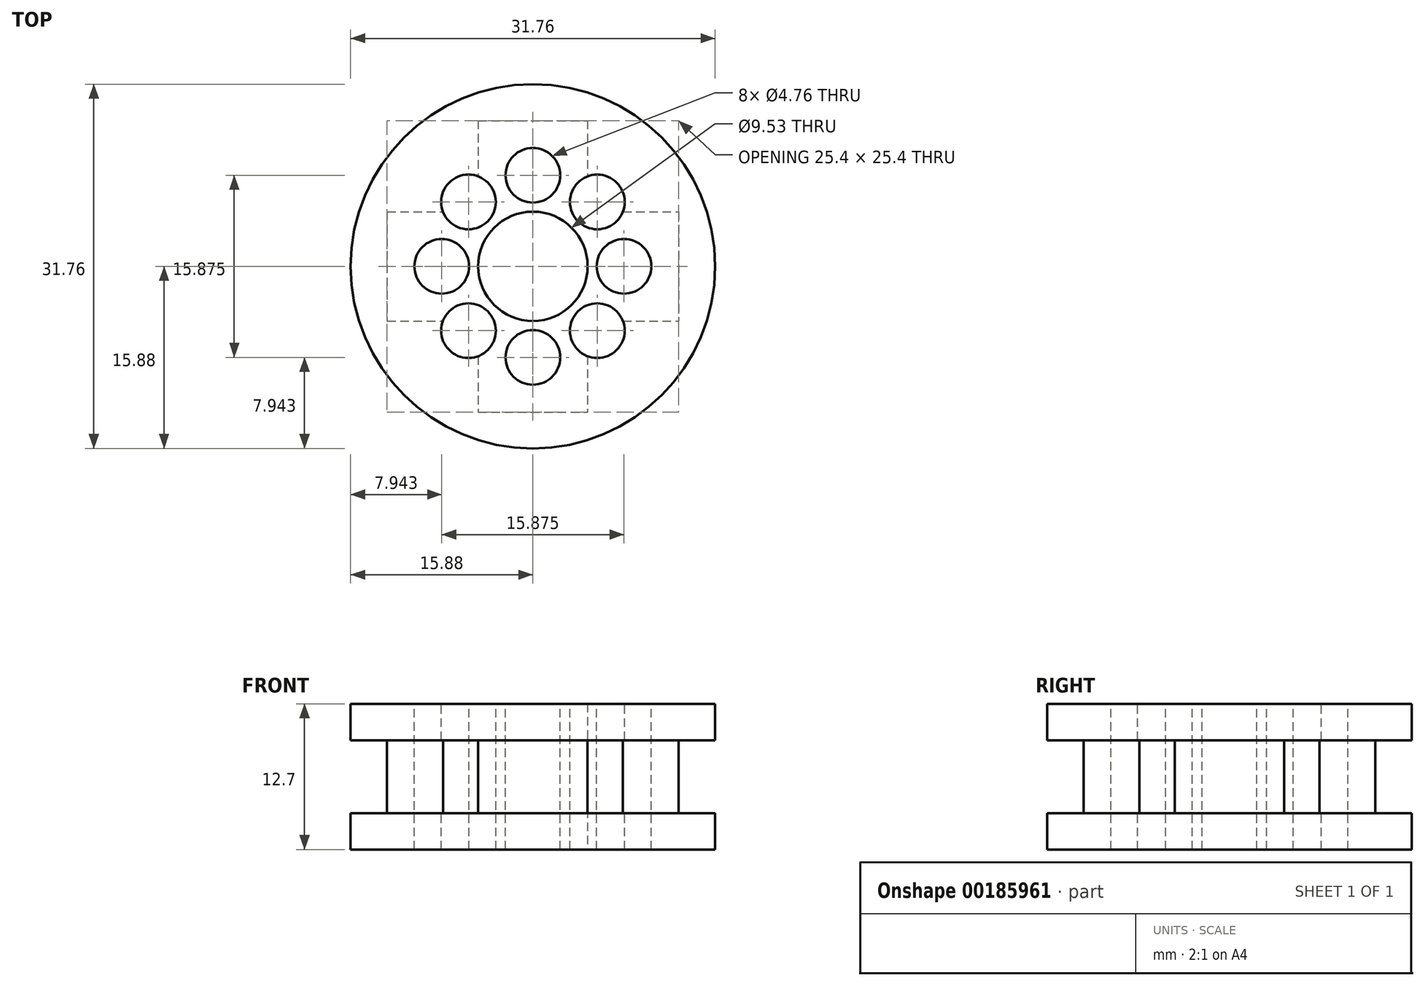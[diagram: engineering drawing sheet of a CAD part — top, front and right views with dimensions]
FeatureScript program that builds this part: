
annotation { "Feature Type Name" : "Feature", "Feature Type Description" : "" }
export const myFeature = defineFeature(function(context is Context, id is Id, definition is map)
    precondition{}
    {
        {
            var Q0;
            Q0=qCreatedBy(makeId("Top.planeOp"),FACE);
            var sketch = newSketch(context, id + "F0", { "sketchPlane" : qUnion([Q0])});
            skCircle(sketch, "E0", {"center": v(0, 0) * mm, "radius": 15.88 * mm});
            skCircle(sketch, "E1", {"center": v(0, 0) * mm, "radius": 4.76 * mm});
            skSolve(sketch);
        }
        {
            var Q0;
            Q0 = qSketchRegion(id + "F0", true);
            extrude(context, id + "F1", {"entities" : qUnion([Q0]), "depth" : 3.17 * mm});
        }
        {
            var Q0;
            Q0=makeQuery(id+"F1.opExtrude","CAP_FACE",FACE,{"disambiguationData":[OSD([sQuery(id+"F0.wireOp",EDGE,"E0"),sQuery(id+"F0.wireOp",EDGE,"E1")])],"isStart":false});
            var sketch = newSketch(context, id + "F2", { "sketchPlane" : qUnion([Q0])});
            skCircle(sketch, "E2", {"center": v(0, 0) * mm, "radius": 4.76 * mm});
            skLineSegment(sketch, "E3.bottom", {"start": v(-4.76, 12.7) * mm, "end": v(4.76, 12.7) * mm});
            skLineSegment(sketch, "E3.top", {"start": v(-4.76, -12.7) * mm, "end": v(4.76, -12.7) * mm});
            skLineSegment(sketch, "E3.left", {"start": v(-4.76, 12.7) * mm, "end": v(-4.76, -12.7) * mm});
            skLineSegment(sketch, "E3.right", {"start": v(4.76, 12.7) * mm, "end": v(4.76, -12.7) * mm});
            skLineSegment(sketch, "E4.bottom", {"start": v(-12.7, 4.76) * mm, "end": v(12.7, 4.76) * mm});
            skLineSegment(sketch, "E4.top", {"start": v(-12.7, -4.76) * mm, "end": v(12.7, -4.76) * mm});
            skLineSegment(sketch, "E4.left", {"start": v(-12.7, 4.76) * mm, "end": v(-12.7, -4.76) * mm});
            skLineSegment(sketch, "E4.right", {"start": v(12.7, 4.76) * mm, "end": v(12.7, -4.76) * mm});
            skSolve(sketch);
        }
        {
            var Q0;
            Q0 = qSketchRegion(id + "F2", true);
            extrude(context, id + "F3", {"entities" : qUnion([Q0]), "operationType" : NewBodyOperationType.ADD, "depth" : 6.35 * mm});
        }
        {
            var Q0;
            Q0=makeQuery(id+"F3.opExtrude","CAP_FACE",FACE,{"disambiguationData":[OSD([sQuery(id+"F2.wireOp",EDGE,"E2"),sQuery(id+"F2.wireOp",EDGE,"E3.bottom"),sQuery(id+"F2.wireOp",EDGE,"E3.top"),sQuery(id+"F2.wireOp",EDGE,"E3.left"),sQuery(id+"F2.wireOp",EDGE,"E3.right"),sQuery(id+"F2.wireOp",EDGE,"E4.bottom"),sQuery(id+"F2.wireOp",EDGE,"E4.top"),sQuery(id+"F2.wireOp",EDGE,"E4.left"),sQuery(id+"F2.wireOp",EDGE,"E4.right")])],"isStart":false});
            var sketch = newSketch(context, id + "F4", { "sketchPlane" : qUnion([Q0])});
            skCircle(sketch, "E5", {"center": v(0, 0) * mm, "radius": 15.88 * mm});
            skCircle(sketch, "E6", {"center": v(0, 0) * mm, "radius": 4.76 * mm});
            skSolve(sketch);
        }
        {
            var Q0;
            Q0 = qSketchRegion(id + "F4", true);
            extrude(context, id + "F5", {"entities" : qUnion([Q0]), "operationType" : NewBodyOperationType.ADD, "depth" : 3.17 * mm});
        }
        {
            var Q0;
            Q0=makeQuery(id+"F5.opExtrude","CAP_FACE",FACE,{"disambiguationData":[OSD([sQuery(id+"F4.wireOp",EDGE,"E5"),sQuery(id+"F4.wireOp",EDGE,"E6")])],"isStart":false});
            var sketch = newSketch(context, id + "F6", { "sketchPlane" : qUnion([Q0])});
            skCircle(sketch, "E7", {"center": v(0, 7.94) * mm, "radius": 2.38 * mm});
            skCircle(sketch, "E8.1.0", {"center": v(-5.61, 5.61) * mm, "radius": 2.38 * mm});
            skCircle(sketch, "E8.2.0", {"center": v(-7.94, 0) * mm, "radius": 2.38 * mm});
            skCircle(sketch, "E8.3.0", {"center": v(-5.61, -5.61) * mm, "radius": 2.38 * mm});
            skCircle(sketch, "E8.4.0", {"center": v(0, -7.94) * mm, "radius": 2.38 * mm});
            skCircle(sketch, "E8.5.0", {"center": v(5.61, -5.61) * mm, "radius": 2.38 * mm});
            skCircle(sketch, "E8.6.0", {"center": v(7.94, 0) * mm, "radius": 2.38 * mm});
            skCircle(sketch, "E8.7.0", {"center": v(5.61, 5.61) * mm, "radius": 2.38 * mm});
            skPoint(sketch, "E8.center", {"position": v(0, 0) * mm});
            skSolve(sketch);
        }
        {
            var Q0;
            Q0=makeQuery(id+"F6.imprint","IMPRINT",FACE,{"disambiguationData":[TD([[makeQuery(id+"F6.imprint","IMPRINT",EDGE,{"derivedFrom":sQuery(id+"F6.wireOp",EDGE,"E8.1.0")}),1.0]])]});
            var Q1;
            Q1=makeQuery(id+"F6.imprint","IMPRINT",FACE,{"disambiguationData":[TD([[makeQuery(id+"F6.imprint","IMPRINT",EDGE,{"derivedFrom":sQuery(id+"F6.wireOp",EDGE,"E7")}),1.0]])]});
            var Q2;
            Q2=makeQuery(id+"F6.imprint","IMPRINT",FACE,{"disambiguationData":[TD([[makeQuery(id+"F6.imprint","IMPRINT",EDGE,{"derivedFrom":sQuery(id+"F6.wireOp",EDGE,"E8.7.0")}),1.0]])]});
            var Q3;
            Q3=makeQuery(id+"F6.imprint","IMPRINT",FACE,{"disambiguationData":[TD([[makeQuery(id+"F6.imprint","IMPRINT",EDGE,{"derivedFrom":sQuery(id+"F6.wireOp",EDGE,"E8.6.0")}),1.0]])]});
            var Q4;
            Q4=makeQuery(id+"F6.imprint","IMPRINT",FACE,{"disambiguationData":[TD([[makeQuery(id+"F6.imprint","IMPRINT",EDGE,{"derivedFrom":sQuery(id+"F6.wireOp",EDGE,"E8.5.0")}),1.0]])]});
            var Q5;
            Q5=makeQuery(id+"F6.imprint","IMPRINT",FACE,{"disambiguationData":[TD([[makeQuery(id+"F6.imprint","IMPRINT",EDGE,{"derivedFrom":sQuery(id+"F6.wireOp",EDGE,"E8.4.0")}),1.0]])]});
            var Q6;
            Q6=makeQuery(id+"F6.imprint","IMPRINT",FACE,{"disambiguationData":[TD([[makeQuery(id+"F6.imprint","IMPRINT",EDGE,{"derivedFrom":sQuery(id+"F6.wireOp",EDGE,"E8.3.0")}),1.0]])]});
            var Q7;
            Q7=makeQuery(id+"F6.imprint","IMPRINT",FACE,{"disambiguationData":[TD([[makeQuery(id+"F6.imprint","IMPRINT",EDGE,{"derivedFrom":sQuery(id+"F6.wireOp",EDGE,"E8.2.0")}),1.0]])]});
            extrude(context, id + "F7", {"entities" : qUnion([Q0, Q1, Q2, Q3, Q4, Q5, Q6, Q7]), "operationType" : NewBodyOperationType.REMOVE, "oppositeDirection" : true, "depth" : 25.4 * mm});
        }
    });
